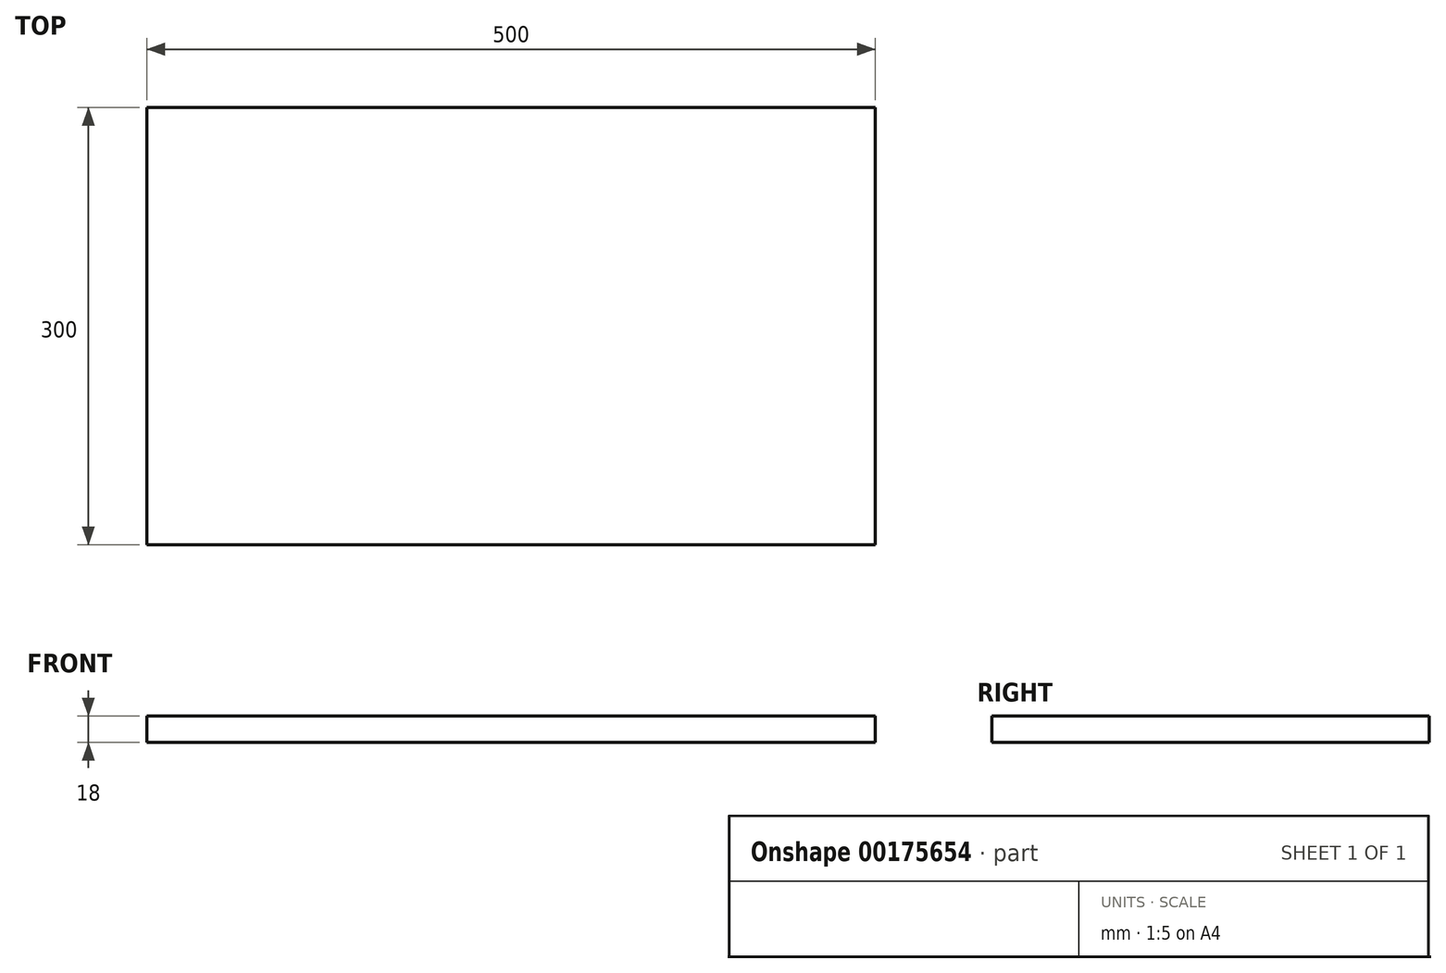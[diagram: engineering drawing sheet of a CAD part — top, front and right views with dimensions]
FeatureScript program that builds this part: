
annotation { "Feature Type Name" : "Feature", "Feature Type Description" : "" }
export const myFeature = defineFeature(function(context is Context, id is Id, definition is map)
    precondition{}
    {
        {
            var Q0;
            Q0=qCreatedBy(makeId("Top.planeOp"),FACE);
            var sketch = newSketch(context, id + "F0", { "sketchPlane" : qUnion([Q0])});
            skLineSegment(sketch, "E0.bottom", {"start": v(-266.16, 227.1) * mm, "end": v(233.84, 227.1) * mm});
            skLineSegment(sketch, "E0.top", {"start": v(-266.16, -72.9) * mm, "end": v(233.84, -72.9) * mm});
            skLineSegment(sketch, "E0.left", {"start": v(-266.16, 227.1) * mm, "end": v(-266.16, -72.9) * mm});
            skLineSegment(sketch, "E0.right", {"start": v(233.84, 227.1) * mm, "end": v(233.84, -72.9) * mm});
            skSolve(sketch);
        }
        {
            var Q0;
            Q0 = qSketchRegion(id + "F0", true);
            extrude(context, id + "F1", {"entities" : qUnion([Q0]), "depth" : 18 * mm});
        }
    });
